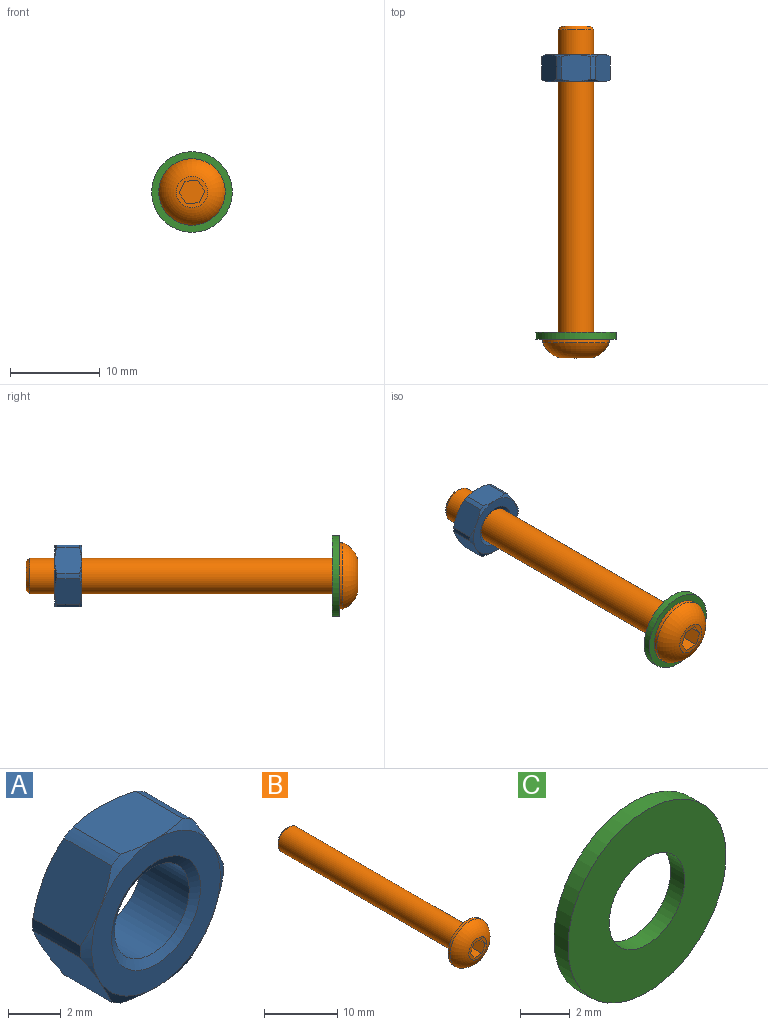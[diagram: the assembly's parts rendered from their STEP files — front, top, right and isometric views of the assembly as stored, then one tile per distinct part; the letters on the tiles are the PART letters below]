
ASSEMBLY  parts=3 mates=2
PART A: 19 faces, bbox 7.7x3x7.7 mm
  f0: cylinder r=3.83mm len=2.56mm, axis (0,-1,0), area 1.5mm2, adj f11,f12,f17,f18
  f1: cylinder r=3.83mm len=2.56mm, axis (0,-1,0), area 1.5mm2, adj f11,f12,f16,f17
  f2: cylinder r=3.83mm len=2.56mm, axis (0,-1,0), area 1.5mm2, adj f11,f12,f15,f16
  f3: cylinder r=3.83mm len=2.56mm, axis (0,-1,0), area 1.5mm2, adj f11,f12,f14,f15
  f4: cylinder r=3.83mm len=2.56mm, axis (0,-1,0), area 1.5mm2, adj f11,f12,f13,f14
  f5: cylinder r=2mm len=4mm, axis (0,-1,0), area 32.1mm2, adj f9,f10
  f6: plane 6.89x6.89mm, normal (0,1,0), area 19.4mm2, adj f9,f11
  f7: cylinder r=3.83mm len=2.56mm, axis (0,-1,0), area 1.5mm2, adj f11,f12,f13,f18
  f8: plane 6.89x6.89mm, normal (0,-1,0), area 19.4mm2, adj f10,f12
  f9: cone r=2.38mm half-angle=60deg, axis (0,1,0), area 6.1mm2, adj f5,f6
  f10: cone r=2mm half-angle=60deg, axis (0,-1,0), area 6.1mm2, adj f5,f8
  f11: cone r=3.83mm half-angle=60deg, axis (0,-1,0), area 4.3mm2, adj f0,f1,f2,f3,f4,f6,f7,f13
  f12: cone r=3.45mm half-angle=60deg, axis (0,1,0), area 4.3mm2, adj f0,f1,f2,f3,f4,f7,f8,f13
  f13: plane 3x2.88mm, normal (-0.87,0,0.5), area 9.5mm2, adj f4,f7,f11,f12
  f14: plane 3x2.88mm, normal (-0.87,0,-0.5), area 9.5mm2, adj f3,f4,f11,f12
  f15: plane 3.33x3mm, normal (0,0,-1), area 9.5mm2, adj f2,f3,f11,f12
  f16: plane 3x2.88mm, normal (0.87,0,-0.5), area 9.5mm2, adj f1,f2,f11,f12
  f17: plane 3x2.88mm, normal (0.87,0,0.5), area 9.5mm2, adj f0,f1,f11,f12
  f18: plane 3.33x3mm, normal (0,0,1), area 9.5mm2, adj f0,f7,f11,f12
PART B: 14 faces, bbox 7.4x37.1x7.4 mm
  f0: plane 3.5x3.5mm, normal (0,-1,0), area 4.2mm2, adj f5,f7,f8,f9,f10,f11,f12
  f1: cone r=2mm half-angle=41.8deg, axis (0,-1,0), area 6.2mm2, adj f2,f6
  f2: cylinder r=2mm len=34.6mm, axis (0,1,0), area 434.7mm2, adj f1,f3
  f3: plane 7.42x7.42mm, normal (0,1,0), area 30.7mm2, adj f2,f4
  f4: cylinder r=3.71mm len=7.42mm, axis (0,1,0), area 9.3mm2, adj f3,f5
  f5: torus R=1.1mm, axis (0,1,0), area 48.2mm2, adj f0,f4
  f6: plane 3.28x3.28mm, normal (0,1,0), area 8.4mm2, adj f1
  f7: plane 2x1.21mm, normal (-0.84,0,-0.55), area 2.9mm2, adj f0,f8,f12,f13
  f8: plane 2x1.44mm, normal (0.06,0,-1), area 2.9mm2, adj f0,f7,f9,f13
  f9: plane 2x1.29mm, normal (0.89,0,-0.45), area 2.9mm2, adj f0,f8,f10,f13
  f10: plane 2x1.21mm, normal (0.84,0,0.55), area 2.9mm2, adj f0,f9,f11,f13
  f11: plane 2x1.44mm, normal (-0.06,0,1), area 2.9mm2, adj f0,f10,f12,f13
  f12: plane 2x1.29mm, normal (-0.89,0,0.45), area 2.9mm2, adj f0,f7,f11,f13
  f13: plane 2.88x2.58mm, normal (0,-1,0), area 5.4mm2, adj f7,f8,f9,f10,f11,f12
PART C: 4 faces, bbox 9x0.8x9 mm
  f0: cylinder r=2.15mm len=4.3mm, axis (0,1,0), area 10.8mm2, adj f2,f3
  f1: cylinder r=4.5mm len=9mm, axis (0,1,0), area 22.6mm2, adj f2,f3
  f2: plane 9x9mm, normal (0,-1,0), area 49.1mm2, adj f0,f1
  f3: plane 9x9mm, normal (0,1,0), area 49.1mm2, adj f0,f1
PLACE A t=(4.03,19.53,-9.63)mm
PLACE B t=(-142.28,2.04,-9.63)mm
PLACE C t=(32.84,-8.47,1.43)mm
MATE fastened C.f0 <-> B.f1  axis (0,-1,0) through (4.03,-9.27,-9.63)mm
MATE fastened C.f0 <-> A.f0  axis (0,1,0) through (4.03,-8.47,-9.63)mm
